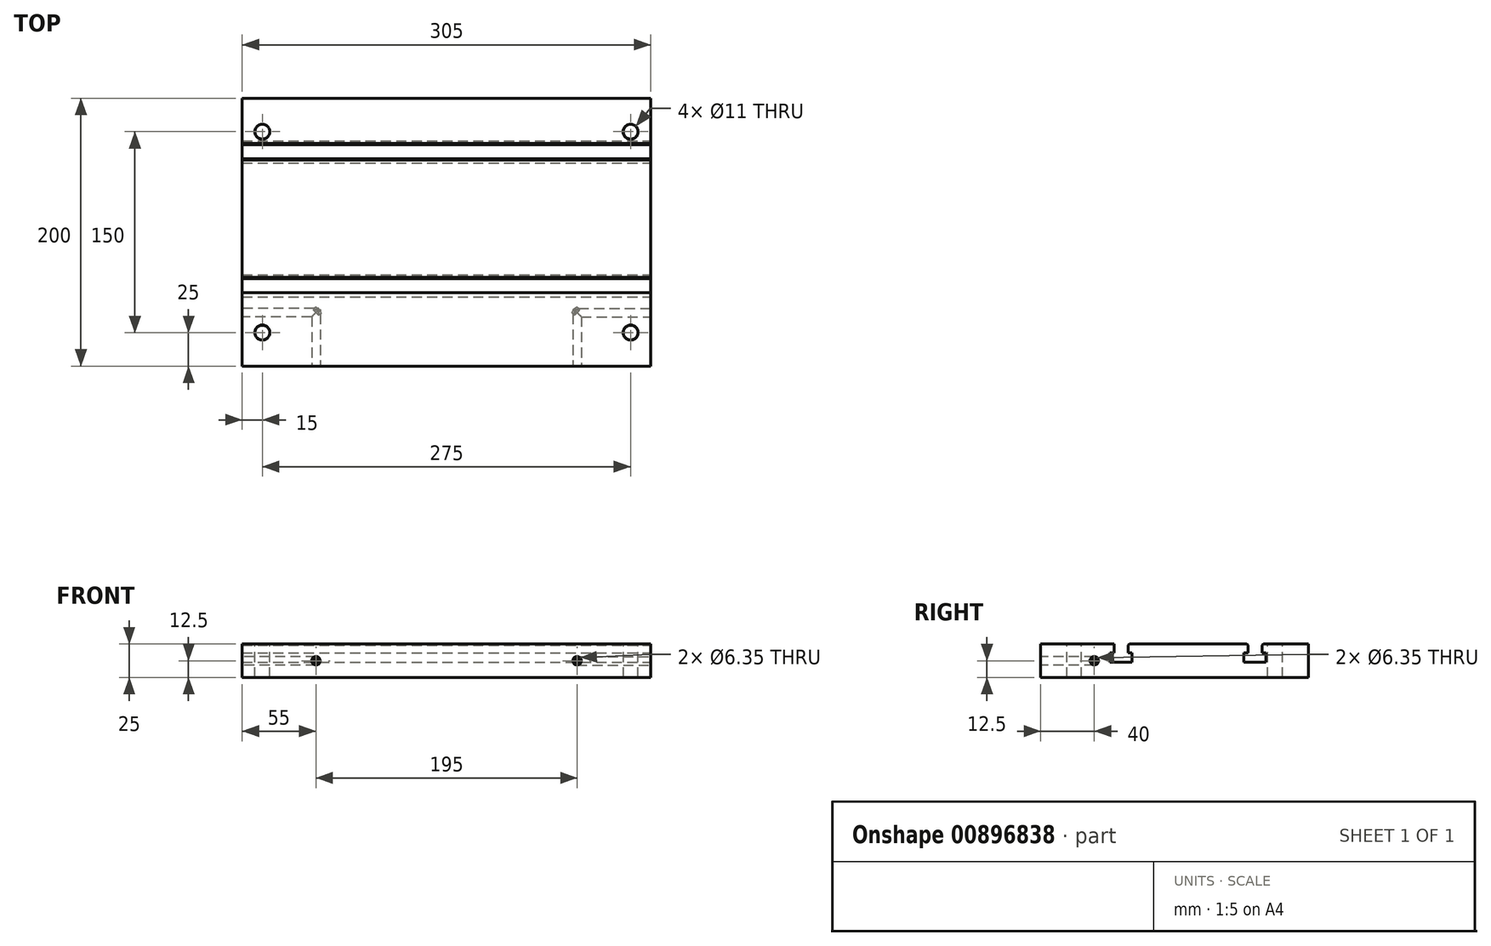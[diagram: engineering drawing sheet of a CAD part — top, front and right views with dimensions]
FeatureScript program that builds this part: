
annotation { "Feature Type Name" : "Feature", "Feature Type Description" : "" }
export const myFeature = defineFeature(function(context is Context, id is Id, definition is map)
    precondition{}
    {
        {
            var Q0;
            Q0=qCreatedBy(makeId("Top.planeOp"),FACE);
            var sketch = newSketch(context, id + "F0", { "sketchPlane" : qUnion([Q0])});
            skLineSegment(sketch, "E0.bottom", {"start": v(-152.5, 100) * mm, "end": v(152.5, 100) * mm});
            skLineSegment(sketch, "E0.top", {"start": v(-152.5, -100) * mm, "end": v(152.5, -100) * mm});
            skLineSegment(sketch, "E0.left", {"start": v(-152.5, 100) * mm, "end": v(-152.5, -100) * mm});
            skLineSegment(sketch, "E0.right", {"start": v(152.5, 100) * mm, "end": v(152.5, -100) * mm});
            skPoint(sketch, "E0.middle", {"position": v(0, 0) * mm});
            skSolve(sketch);
        }
        {
            var Q0;
            Q0=makeQuery(id+"F0.imprint","IMPRINT",FACE,{"disambiguationData":[TD([[makeQuery(id+"F0.imprint","IMPRINT",EDGE,{"derivedFrom":sQuery(id+"F0.wireOp",EDGE,"E0.bottom")}),-1.0]])]});
            extrude(context, id + "F1", {"entities" : qUnion([Q0]), "oppositeDirection" : true, "depth" : 25 * mm, "offsetDistance" : 25 * mm});
        }
        {
            var Q0;
            Q0=makeQuery(id+"F1.opExtrude","CAP_FACE",FACE,{"disambiguationData":[OSD([sQuery(id+"F0.wireOp",EDGE,"E0.bottom"),sQuery(id+"F0.wireOp",EDGE,"E0.top"),sQuery(id+"F0.wireOp",EDGE,"E0.left"),sQuery(id+"F0.wireOp",EDGE,"E0.right")])],"isStart":true});
            var sketch = newSketch(context, id + "F2", { "sketchPlane" : qUnion([Q0])});
            skLineSegment(sketch, "E1.bottom", {"start": v(-137.5, 75) * mm, "end": v(137.5, 75) * mm, "construction": true});
            skLineSegment(sketch, "E1.top", {"start": v(-137.5, -75) * mm, "end": v(137.5, -75) * mm, "construction": true});
            skLineSegment(sketch, "E1.left", {"start": v(-137.5, 75) * mm, "end": v(-137.5, -75) * mm, "construction": true});
            skLineSegment(sketch, "E1.right", {"start": v(137.5, 75) * mm, "end": v(137.5, -75) * mm, "construction": true});
            skPoint(sketch, "E1.middle", {"position": v(0, 0) * mm});
            skSolve(sketch);
        }
        {
            var Q0;
            Q0=sQuery(id+"F2.wireOp",VERTEX,"E1.bottom.start");
            var Q1;
            Q1=sQuery(id+"F2.wireOp",VERTEX,"E1.bottom.end");
            var Q2;
            Q2=sQuery(id+"F2.wireOp",VERTEX,"E1.top.end");
            var Q3;
            Q3=sQuery(id+"F2.wireOp",VERTEX,"E1.top.start");
            var Q4;
            Q4=makeQuery(id+"F1.opExtrude","SWEPT_BODY",BODY,{"disambiguationData":[OSD([sQuery(id+"F0.wireOp",EDGE,"E0.bottom"),sQuery(id+"F0.wireOp",EDGE,"E0.top"),sQuery(id+"F0.wireOp",EDGE,"E0.left"),sQuery(id+"F0.wireOp",EDGE,"E0.right")])]});
            hole(context, id + "F3", {"style" : HoleStyle.C_SINK, "endStyle" : HoleEndStyle.THROUGH, "holeDiameter" : 11 * mm, "cSinkDiameter" : 11.25 * mm, "cSinkAngle" : 90 * degree, "majorDiameter" : 10 * mm, "isTappedThrough" : true, "tappedDepth" : 12 * mm, "tapClearance" : 3, "locations" : qUnion([Q0, Q1, Q2, Q3]), "scope" : qUnion([Q4])});
        }
        {
            var Q0;
            Q0=qCreatedBy(makeId("Right.planeOp"),FACE);
            var sketch = newSketch(context, id + "F4", { "sketchPlane" : qUnion([Q0])});
            skLineSegment(sketch, "E2", {"start": v(-40, 0) * mm, "end": v(-40, -25) * mm, "construction": true});
            skLineSegment(sketch, "E3", {"start": v(-40, 0) * mm, "end": v(-34.75, 0) * mm});
            skLineSegment(sketch, "E4", {"start": v(-34.75, 0) * mm, "end": v(-34.75, -6.5) * mm});
            skLineSegment(sketch, "E5", {"start": v(-34.75, -6.5) * mm, "end": v(-31.75, -6.5) * mm});
            skLineSegment(sketch, "E6", {"start": v(-31.75, -6.5) * mm, "end": v(-31.75, -13.5) * mm});
            skLineSegment(sketch, "E7", {"start": v(-31.75, -13.5) * mm, "end": v(-40, -13.5) * mm});
            skLineSegment(sketch, "E8.MirrorCS", {"start": v(-40, 0) * mm, "end": v(-45.25, 0) * mm});
            skLineSegment(sketch, "E9.MirrorCS", {"start": v(-45.25, 0) * mm, "end": v(-45.25, -6.5) * mm});
            skLineSegment(sketch, "E10.MirrorCS", {"start": v(-45.25, -6.5) * mm, "end": v(-48.25, -6.5) * mm});
            skLineSegment(sketch, "E11.MirrorCS", {"start": v(-48.25, -6.5) * mm, "end": v(-48.25, -13.5) * mm});
            skLineSegment(sketch, "E12.MirrorCS", {"start": v(-48.25, -13.5) * mm, "end": v(-40, -13.5) * mm});
            skLineSegment(sketch, "E13", {"start": v(60, 0) * mm, "end": v(60, -25) * mm, "construction": true});
            skLineSegment(sketch, "E14", {"start": v(60, 0) * mm, "end": v(65.25, 0) * mm});
            skLineSegment(sketch, "E15", {"start": v(65.25, 0) * mm, "end": v(65.25, -6.5) * mm});
            skLineSegment(sketch, "E16", {"start": v(65.25, -6.5) * mm, "end": v(68.25, -6.5) * mm});
            skLineSegment(sketch, "E17", {"start": v(68.25, -6.5) * mm, "end": v(68.25, -13.5) * mm});
            skLineSegment(sketch, "E18", {"start": v(68.25, -13.5) * mm, "end": v(60, -13.5) * mm});
            skLineSegment(sketch, "E19.MirrorCS", {"start": v(60, 0) * mm, "end": v(54.75, 0) * mm});
            skLineSegment(sketch, "E20.MirrorCS", {"start": v(54.75, 0) * mm, "end": v(54.75, -6.5) * mm});
            skLineSegment(sketch, "E21.MirrorCS", {"start": v(54.75, -6.5) * mm, "end": v(51.75, -6.5) * mm});
            skLineSegment(sketch, "E22.MirrorCS", {"start": v(51.75, -6.5) * mm, "end": v(51.75, -13.5) * mm});
            skLineSegment(sketch, "E23.MirrorCS", {"start": v(51.75, -13.5) * mm, "end": v(60, -13.5) * mm});
            skSolve(sketch);
        }
        {
            var Q0;
            Q0=qSketchRegion(id+"F4",true);
            extrude(context, id + "F5", {"entities" : qUnion([Q0]), "operationType" : NewBodyOperationType.REMOVE, "endBound" : BoundingType.THROUGH_ALL, "oppositeDirection" : true, "depth" : 25 * mm, "offsetDistance" : 25 * mm, "hasSecondDirection" : true, "secondDirectionBound" : SecondDirectionBoundingType.THROUGH_ALL, "secondDirectionOppositeDirection" : false, "secondDirectionDepth" : 25 * mm});
        }
        {
            var Q0;
            Q0=makeQuery(id+"F5.boolean.opBoolean","COPY",EDGE,{"derivedFrom":makeQuery(id+"F5.opExtrude","SWEPT_EDGE",EDGE,{"disambiguationData":[OSD([sQuery(id+"F4.wireOp",EDGE,"E3"),sQuery(id+"F4.wireOp",EDGE,"E4")])]})});
            var Q1;
            Q1=makeQuery(id+"F5.boolean.opBoolean","COPY",EDGE,{"derivedFrom":makeQuery(id+"F5.opExtrude","SWEPT_EDGE",EDGE,{"disambiguationData":[OSD([sQuery(id+"F4.wireOp",EDGE,"E8.MirrorCS"),sQuery(id+"F4.wireOp",EDGE,"E9.MirrorCS")])]})});
            var Q2;
            Q2=makeQuery(id+"F5.boolean.opBoolean","COPY",EDGE,{"derivedFrom":makeQuery(id+"F5.opExtrude","SWEPT_EDGE",EDGE,{"disambiguationData":[OSD([sQuery(id+"F4.wireOp",EDGE,"E14"),sQuery(id+"F4.wireOp",EDGE,"E15")])]})});
            var Q3;
            Q3=makeQuery(id+"F5.boolean.opBoolean","COPY",EDGE,{"derivedFrom":makeQuery(id+"F5.opExtrude","SWEPT_EDGE",EDGE,{"disambiguationData":[OSD([sQuery(id+"F4.wireOp",EDGE,"E19.MirrorCS"),sQuery(id+"F4.wireOp",EDGE,"E20.MirrorCS")])]})});
            chamfer(context, id + "F6", {"entities" : qUnion([Q0, Q1, Q2, Q3]), "width" : 1 * mm, "tangentPropagation" : true});
        }
        {
            var Q0;
            Q0=makeQuery(id+"F1.opExtrude","SWEPT_FACE",FACE,{"disambiguationData":[OSD([sQuery(id+"F0.wireOp",EDGE,"E0.left")])]});
            var sketch = newSketch(context, id + "F7", { "sketchPlane" : qUnion([Q0])});
            skPoint(sketch, "E24", {"position": v(60, -12.5) * mm});
            skSolve(sketch);
        }
        {
            var Q0;
            Q0=makeQuery(id+"F1.opExtrude","SWEPT_FACE",FACE,{"disambiguationData":[OSD([sQuery(id+"F0.wireOp",EDGE,"E0.right")])]});
            var sketch = newSketch(context, id + "F8", { "sketchPlane" : qUnion([Q0])});
            skPoint(sketch, "E25.0", {"position": v(-60, -12.5) * mm});
            skSolve(sketch);
        }
        {
            var Q0;
            Q0=makeQuery(id+"F1.opExtrude","SWEPT_FACE",FACE,{"disambiguationData":[OSD([sQuery(id+"F0.wireOp",EDGE,"E0.top")])]});
            var sketch = newSketch(context, id + "F9", { "sketchPlane" : qUnion([Q0])});
            skPoint(sketch, "E26", {"position": v(-97.5, -12.5) * mm});
            skPoint(sketch, "E27.MirrorP", {"position": v(97.5, -12.5) * mm});
            skSolve(sketch);
        }
        {
            var Q0;
            Q0=sQuery(id+"F9.wireOp",VERTEX,"E27.MirrorP");
            var Q1;
            Q1=sQuery(id+"F9.wireOp",VERTEX,"E26");
            var Q2;
            Q2=makeQuery(id+"F1.opExtrude","SWEPT_BODY",BODY,{"disambiguationData":[OSD([sQuery(id+"F0.wireOp",EDGE,"E0.bottom"),sQuery(id+"F0.wireOp",EDGE,"E0.top"),sQuery(id+"F0.wireOp",EDGE,"E0.left"),sQuery(id+"F0.wireOp",EDGE,"E0.right")])]});
            hole(context, id + "F10", {"style" : HoleStyle.SIMPLE, "endStyle" : HoleEndStyle.BLIND, "holeDiameter" : 6.35 * mm, "majorDiameter" : 10 * mm, "holeDepth" : 42 * mm, "isTappedThrough" : true, "tappedDepth" : 12 * mm, "tapClearance" : 3, "locations" : qUnion([Q0, Q1]), "scope" : qUnion([Q2])});
        }
        {
            var Q0;
            Q0=sQuery(id+"F7.wireOp",VERTEX,"E24");
            var Q1;
            Q1=sQuery(id+"F8.wireOp",VERTEX,"E25.0");
            var Q2;
            Q2=makeQuery(id+"F1.opExtrude","SWEPT_BODY",BODY,{"disambiguationData":[OSD([sQuery(id+"F0.wireOp",EDGE,"E0.bottom"),sQuery(id+"F0.wireOp",EDGE,"E0.top"),sQuery(id+"F0.wireOp",EDGE,"E0.left"),sQuery(id+"F0.wireOp",EDGE,"E0.right")])]});
            hole(context, id + "F11", {"style" : HoleStyle.SIMPLE, "endStyle" : HoleEndStyle.BLIND, "holeDiameter" : 6.35 * mm, "majorDiameter" : 5 * mm, "holeDepth" : 57 * mm, "isTappedThrough" : true, "tappedDepth" : 12 * mm, "tapClearance" : 3, "locations" : qUnion([Q0, Q1]), "scope" : qUnion([Q2])});
        }
    });
